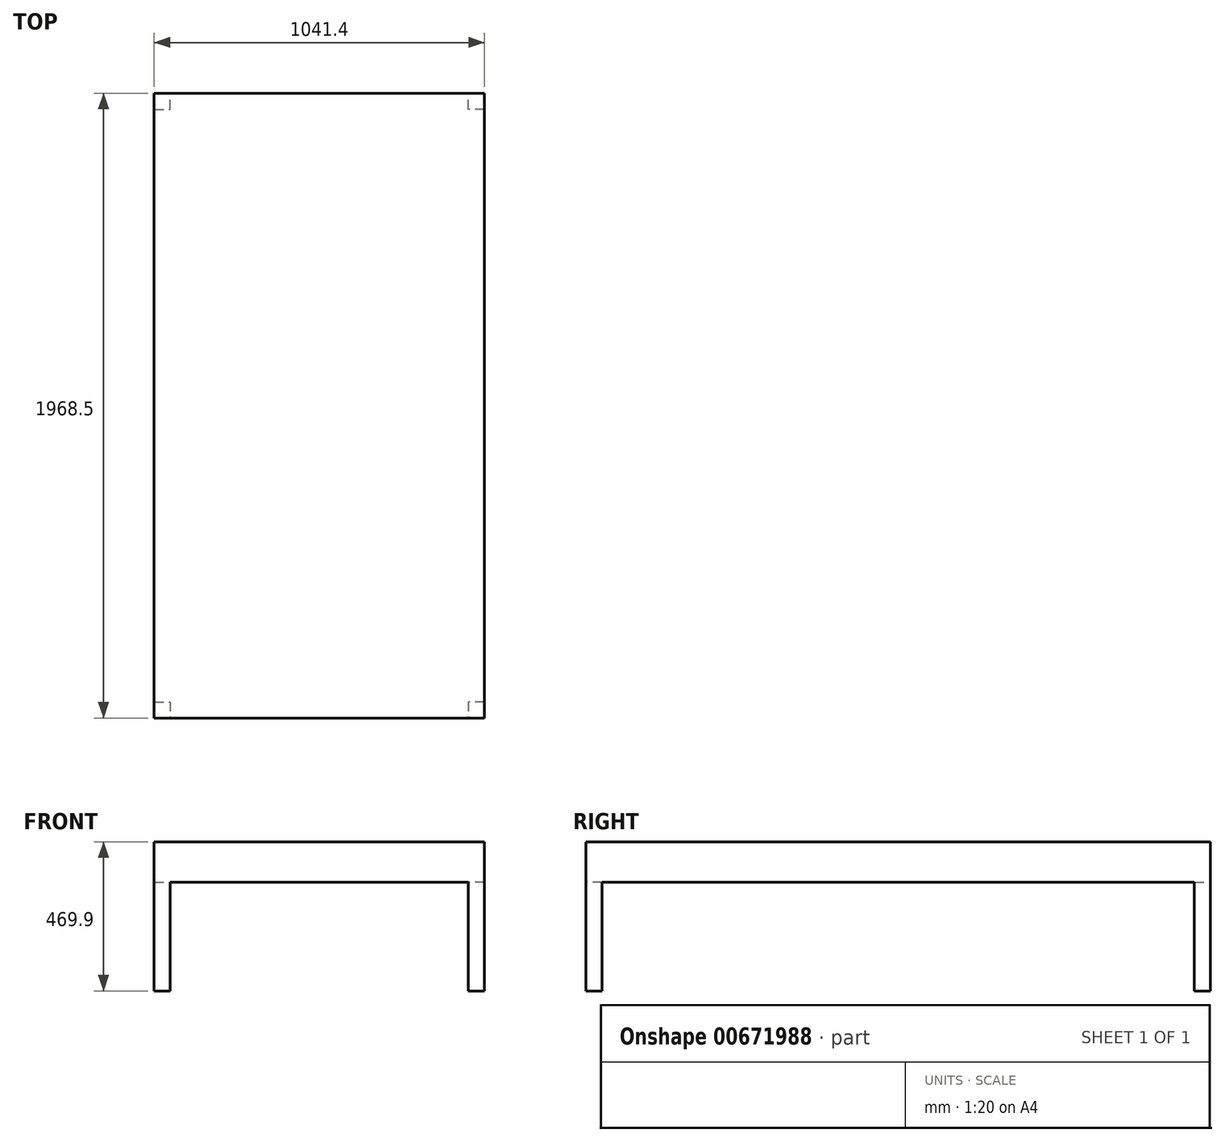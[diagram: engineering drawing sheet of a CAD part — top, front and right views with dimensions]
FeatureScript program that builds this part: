
annotation { "Feature Type Name" : "Feature", "Feature Type Description" : "" }
export const myFeature = defineFeature(function(context is Context, id is Id, definition is map)
    precondition{}
    {
        {
            var Q0;
            Q0=qCreatedBy(makeId("Top.planeOp"),FACE);
            var sketch = newSketch(context, id + "F0", { "sketchPlane" : qUnion([Q0])});
            skLineSegment(sketch, "E0.bottom", {"start": v(520.7, 984.25) * mm, "end": v(-520.7, 984.25) * mm});
            skLineSegment(sketch, "E0.top", {"start": v(520.7, -984.25) * mm, "end": v(-520.7, -984.25) * mm});
            skLineSegment(sketch, "E0.left", {"start": v(520.7, 984.25) * mm, "end": v(520.7, -984.25) * mm});
            skLineSegment(sketch, "E0.right", {"start": v(-520.7, 984.25) * mm, "end": v(-520.7, -984.25) * mm});
            skPoint(sketch, "E0.middle", {"position": v(0, 0) * mm});
            skSolve(sketch);
        }
        {
            var Q0;
            Q0=makeQuery(id+"F0.imprint","IMPRINT",FACE,{"disambiguationData":[TD([[makeQuery(id+"F0.imprint","IMPRINT",EDGE,{"derivedFrom":sQuery(id+"F0.wireOp",EDGE,"E0.bottom")}),1.0]])]});
            extrude(context, id + "F1", {"entities" : qUnion([Q0]), "depth" : 127 * mm, "offsetDistance" : 25.4 * mm});
        }
        {
            var Q0;
            Q0=makeQuery(id+"F1.opExtrude","CAP_FACE",FACE,{"disambiguationData":[OSD([sQuery(id+"F0.wireOp",EDGE,"E0.bottom"),sQuery(id+"F0.wireOp",EDGE,"E0.top"),sQuery(id+"F0.wireOp",EDGE,"E0.left"),sQuery(id+"F0.wireOp",EDGE,"E0.right")])],"isStart":true});
            var sketch = newSketch(context, id + "F2", { "sketchPlane" : qUnion([Q0])});
            skLineSegment(sketch, "E1.bottom", {"start": v(-520.7, 933.45) * mm, "end": v(-469.9, 933.45) * mm});
            skLineSegment(sketch, "E1.top", {"start": v(-520.7, 984.25) * mm, "end": v(-469.9, 984.25) * mm});
            skLineSegment(sketch, "E1.left", {"start": v(-520.7, 933.45) * mm, "end": v(-520.7, 984.25) * mm});
            skLineSegment(sketch, "E1.right", {"start": v(-469.9, 933.45) * mm, "end": v(-469.9, 984.25) * mm});
            skLineSegment(sketch, "E2", {"start": v(0, 984.25) * mm, "end": v(0, 0) * mm, "construction": true});
            skLineSegment(sketch, "E3", {"start": v(0, 0) * mm, "end": v(-520.7, 0) * mm, "construction": true});
            skLineSegment(sketch, "E4.MirrorCS", {"start": v(520.7, 933.45) * mm, "end": v(520.7, 984.25) * mm});
            skLineSegment(sketch, "E5.MirrorCS", {"start": v(469.9, 933.45) * mm, "end": v(469.9, 984.25) * mm});
            skLineSegment(sketch, "E6.MirrorCS", {"start": v(520.7, 933.45) * mm, "end": v(469.9, 933.45) * mm});
            skLineSegment(sketch, "E7.MirrorCS", {"start": v(520.7, 984.25) * mm, "end": v(469.9, 984.25) * mm});
            skLineSegment(sketch, "E8.MirrorCS", {"start": v(469.9, -933.45) * mm, "end": v(469.9, -984.25) * mm});
            skLineSegment(sketch, "E9.MirrorCS", {"start": v(520.7, -933.45) * mm, "end": v(469.9, -933.45) * mm});
            skLineSegment(sketch, "E10.MirrorCS", {"start": v(520.7, -984.25) * mm, "end": v(469.9, -984.25) * mm});
            skLineSegment(sketch, "E11.MirrorCS", {"start": v(520.7, -933.45) * mm, "end": v(520.7, -984.25) * mm});
            skLineSegment(sketch, "E12.MirrorCS", {"start": v(-520.7, -984.25) * mm, "end": v(-469.9, -984.25) * mm});
            skLineSegment(sketch, "E13.MirrorCS", {"start": v(-469.9, -933.45) * mm, "end": v(-469.9, -984.25) * mm});
            skLineSegment(sketch, "E14.MirrorCS", {"start": v(-520.7, -933.45) * mm, "end": v(-520.7, -984.25) * mm});
            skLineSegment(sketch, "E15", {"start": v(-520.7, -933.45) * mm, "end": v(-469.9, -933.45) * mm});
            skSolve(sketch);
        }
        {
            var Q0;
            Q0 = qSketchRegion(id + "F2", true);
            extrude(context, id + "F3", {"entities" : qUnion([Q0]), "operationType" : NewBodyOperationType.ADD, "depth" : 342.9 * mm, "offsetDistance" : 25.4 * mm});
        }
    });
